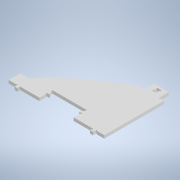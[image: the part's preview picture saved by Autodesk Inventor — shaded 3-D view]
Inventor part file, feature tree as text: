
AUTODESK INVENTOR PART (.ipt)
format: ipt  version: 2020 (Build 240168000, 168)  size: 280,576 bytes
history: native  units: mm
features: extrude x1, sketch x1
ambient origin geometry x8: Origin, YZ Plane, XZ Plane, XY Plane, X Axis, Y Axis, Z Axis, Center Point
bodies: Body1 (feature_tree)
feature tree (2):
  extrude  "Extrusion5"  Depth=6.0mm
  sketch  "Sketch1"  dims[d99=181.29mm d105=32.04mm d106=10.0mm d170=13.004821mm d173=6.0mm d174=5.5mm d202=6.0mm d203=1.333333mm d204=1.333333mm d208=191.29mm d209=2.666667mm d210=2.666667mm d212=14.47956mm d213=61.341583mm d214=145.0mm d223=38.198366mm d226=61.341583mm d232=2.666667mm d233=2.666667mm d235=60.0deg d236=33.288886mm d238=68.606834mm d239=33.288886mm d242=119.5mm d243=7.333333mm d244=2.666667mm d245=20.0mm d246=1.333333mm d247=5.5mm d248=4.5mm d249=6.5mm d250=3.25mm d251=10.0mm d252=2.666667mm d253=2.666667mm d254=2.666667mm d255=2.666667mm d256=425.0mm d257=6.0mm d258=0.0mm d192=0.5mm d193=0.872665mm d194=0.5mm d195=0.872665mm]
